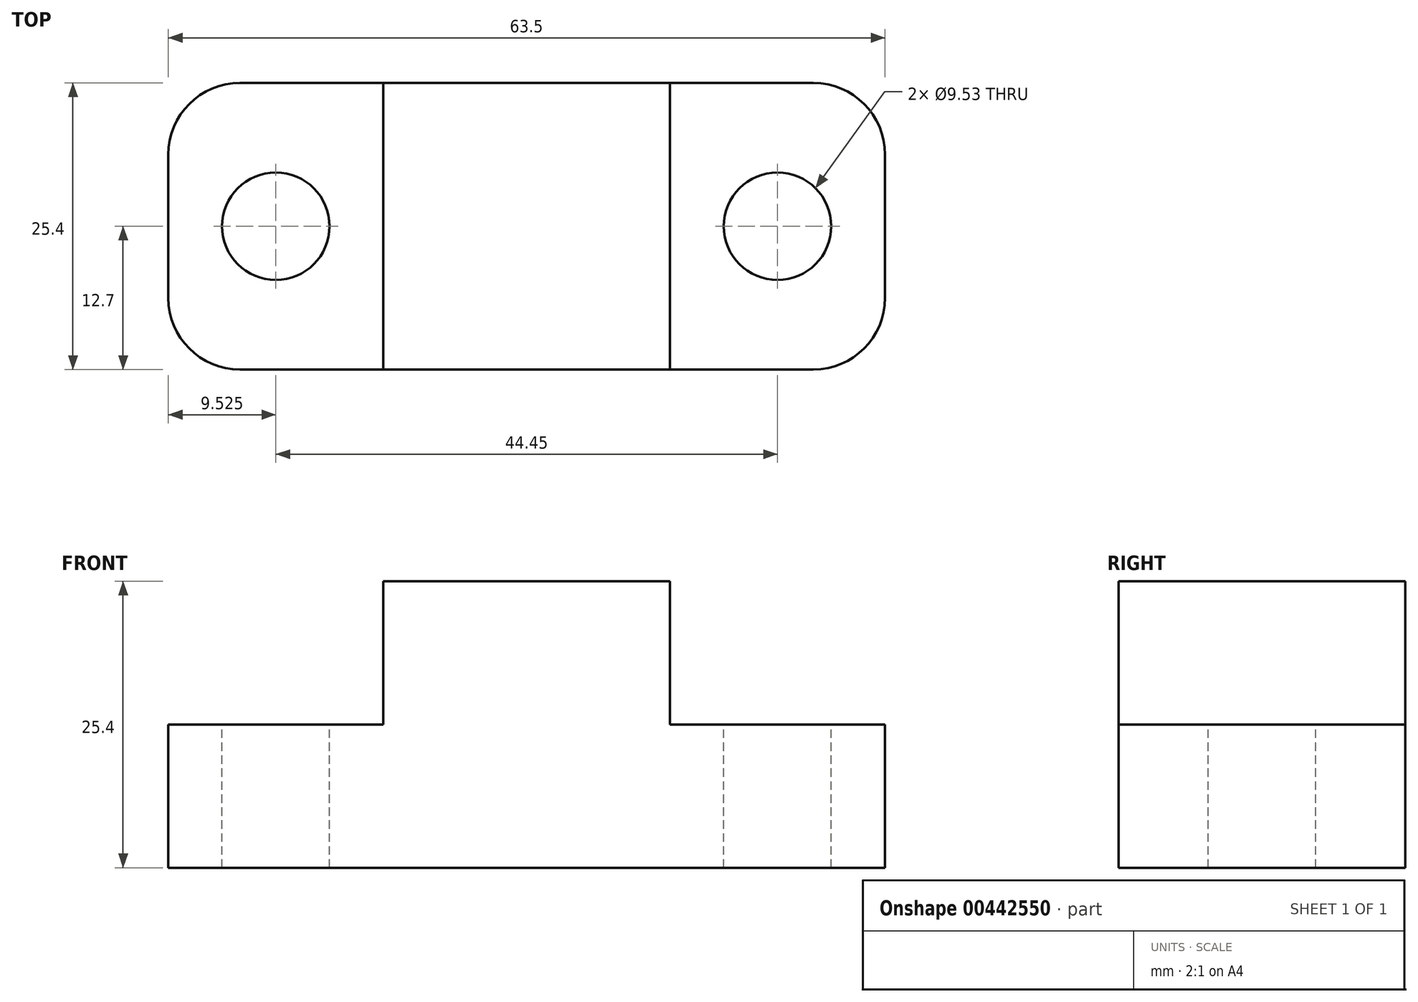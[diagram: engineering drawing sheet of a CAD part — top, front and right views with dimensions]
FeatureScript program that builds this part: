
annotation { "Feature Type Name" : "Feature", "Feature Type Description" : "" }
export const myFeature = defineFeature(function(context is Context, id is Id, definition is map)
    precondition{}
    {
        {
            var Q0;
            Q0=qCreatedBy(makeId("Front.planeOp"),FACE);
            var sketch = newSketch(context, id + "F0", { "sketchPlane" : qUnion([Q0])});
            skLineSegment(sketch, "E0.bottom", {"start": v(-19.05, 0) * mm, "end": v(0, 0) * mm});
            skLineSegment(sketch, "E0.top", {"start": v(-19.05, -12.7) * mm, "end": v(12.7, -12.7) * mm});
            skLineSegment(sketch, "E0.left", {"start": v(-19.05, 0) * mm, "end": v(-19.05, -12.7) * mm});
            skLineSegment(sketch, "E0.right", {"start": v(12.7, 0) * mm, "end": v(12.7, -12.7) * mm});
            skLineSegment(sketch, "E1.top", {"start": v(0, 12.7) * mm, "end": v(12.7, 12.7) * mm});
            skLineSegment(sketch, "E1.left", {"start": v(0, 0) * mm, "end": v(0, 12.7) * mm});
            skLineSegment(sketch, "E1.right", {"start": v(12.7, 0) * mm, "end": v(12.7, 12.7) * mm});
            skSolve(sketch);
        }
        {
            var Q0;
            Q0 = qSketchRegion(id + "F0", true);
            extrude(context, id + "F1", {"entities" : qUnion([Q0]), "oppositeDirection" : true, "depth" : 25.4 * mm});
        }
        {
            var Q0;
            Q0=qCreatedBy(makeId("Top.planeOp"),FACE);
            var sketch = newSketch(context, id + "F2", { "sketchPlane" : qUnion([Q0])});
            skLineSegment(sketch, "E2", {"start": v(-9.53, 25.4) * mm, "end": v(-9.52, 0) * mm, "construction": true});
            skLineSegment(sketch, "E3", {"start": v(0, 12.7) * mm, "end": v(-38.1, 12.7) * mm, "construction": true});
            skPoint(sketch, "E4", {"position": v(-9.52, 12.7) * mm});
            skSolve(sketch);
        }
        {
            var Q0;
            Q0=sQuery(id+"F2.wireOp",VERTEX,"E4");
            var Q1;
            Q1=makeQuery(id+"F1.opExtrude","SWEPT_BODY",BODY,{"disambiguationData":[OSD([sQuery(id+"F0.wireOp",EDGE,"E0.bottom"),sQuery(id+"F0.wireOp",EDGE,"E0.top"),sQuery(id+"F0.wireOp",EDGE,"E0.left"),sQuery(id+"F0.wireOp",EDGE,"E0.right"),sQuery(id+"F0.wireOp",EDGE,"E1.top"),sQuery(id+"F0.wireOp",EDGE,"E1.left"),sQuery(id+"F0.wireOp",EDGE,"E1.right")])]});
            hole(context, id + "F3", {"style" : HoleStyle.SIMPLE, "endStyle" : HoleEndStyle.THROUGH, "holeDiameter" : 9.52 * mm, "isTappedThrough" : true, "tappedDepth" : 12.7 * mm, "tapClearance" : 3, "locations" : qUnion([Q0]), "scope" : qUnion([Q1])});
        }
        {
            var Q0;
            Q0=makeQuery(id+"F1.opExtrude","CAP_EDGE",EDGE,{"disambiguationData":[OSD([sQuery(id+"F0.wireOp",EDGE,"E0.left")])],"isStart":false});
            var Q1;
            Q1=makeQuery(id+"F1.opExtrude","CAP_EDGE",EDGE,{"disambiguationData":[OSD([sQuery(id+"F0.wireOp",EDGE,"E0.left")])],"isStart":true});
            fillet(context, id + "F4", {"entities" : qUnion([Q0, Q1]), "radius" : 6.35 * mm, "tangentPropagation" : true, "allowEdgeOverflow" : false});
        }
        {
            var Q0;
            Q0=makeQuery(id+"F1.opExtrude","SWEPT_BODY",BODY,{"disambiguationData":[OSD([sQuery(id+"F0.wireOp",EDGE,"E0.bottom"),sQuery(id+"F0.wireOp",EDGE,"E0.top"),sQuery(id+"F0.wireOp",EDGE,"E0.left"),sQuery(id+"F0.wireOp",EDGE,"E0.right"),sQuery(id+"F0.wireOp",EDGE,"E1.top"),sQuery(id+"F0.wireOp",EDGE,"E1.left"),sQuery(id+"F0.wireOp",EDGE,"E1.right")])]});
            var Q1;
            Q1=makeQuery(id+"F1.opExtrude","SWEPT_FACE",FACE,{"disambiguationData":[OSD([sQuery(id+"F0.wireOp",EDGE,"E0.right"),sQuery(id+"F0.wireOp",EDGE,"E1.right")])]});
            mirror(context, id + "F5", {"operationType" : NewBodyOperationType.ADD, "entities" : qUnion([Q0]), "mirrorPlane" : qUnion([Q1])});
        }
    });
